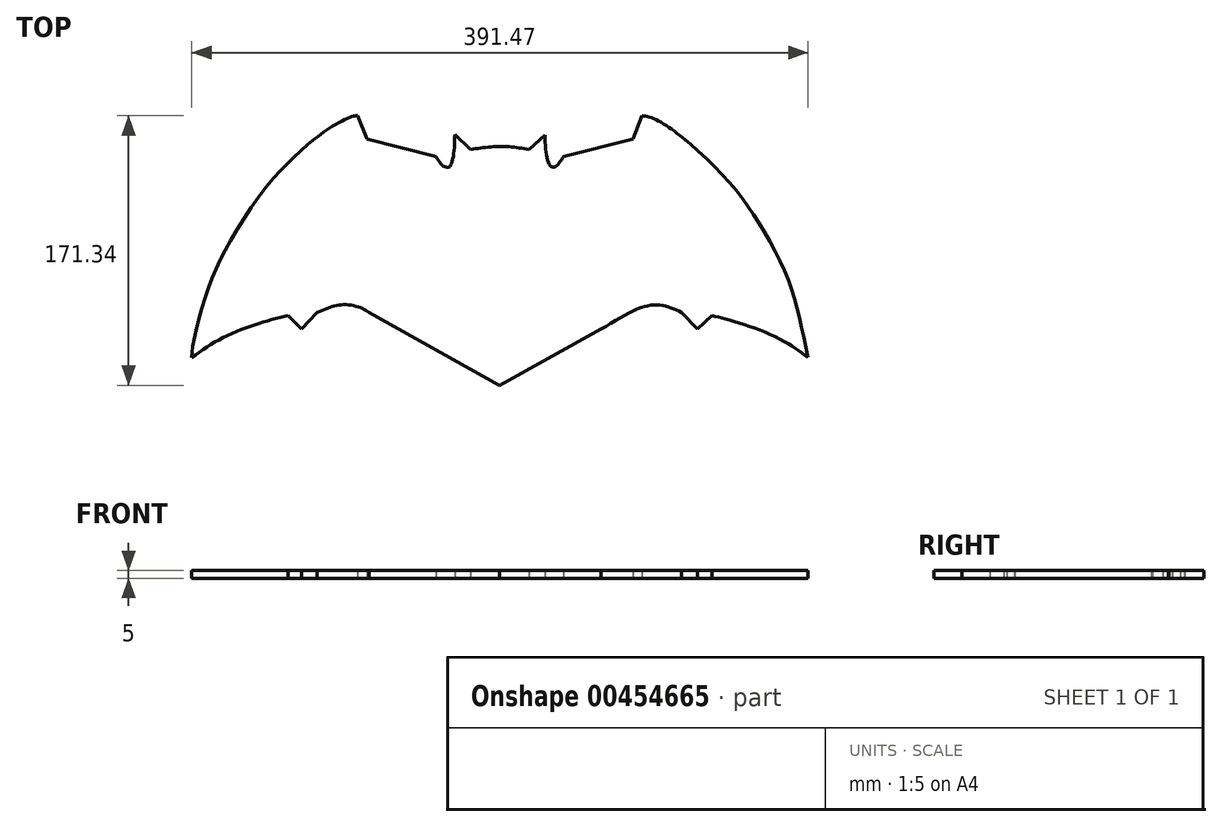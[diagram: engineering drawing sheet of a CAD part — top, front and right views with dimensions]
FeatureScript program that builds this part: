
annotation { "Feature Type Name" : "Feature", "Feature Type Description" : "" }
export const myFeature = defineFeature(function(context is Context, id is Id, definition is map)
    precondition{}
    {
        {
            var Q0;
            Q0=qCreatedBy(makeId("Top.planeOp"),FACE);
            var sketch = newSketch(context, id + "F0", { "sketchPlane" : qUnion([Q0])});
            skLineSegment(sketch, "E0", {"start": v(90.7, 97.95) * mm, "end": v(85.03, 83.2) * mm});
            skLineSegment(sketch, "E1", {"start": v(-84.14, 83.2) * mm, "end": v(-90.13, 97.95) * mm});
            skLineSegment(sketch, "E2", {"start": v(85.03, 83.2) * mm, "end": v(40.87, 72.04) * mm});
            skLineSegment(sketch, "E3", {"start": v(-84.14, 83.2) * mm, "end": v(-40.32, 72.04) * mm});
            skLineSegment(sketch, "E4", {"start": v(-28.3, 85.83) * mm, "end": v(-18.16, 76.47) * mm});
            skLineSegment(sketch, "E5", {"start": v(18.86, 76.47) * mm, "end": v(28.95, 85.66) * mm});
            skLineSegment(sketch, "E6", {"start": v(-125.72, -37.72) * mm, "end": v(-134.3, -29.02) * mm});
            skLineSegment(sketch, "E7", {"start": v(-125.72, -37.72) * mm, "end": v(-115.64, -27.08) * mm});
            skLineSegment(sketch, "E8", {"start": v(-82.75, -27.08) * mm, "end": v(0, -73.39) * mm});
            skLineSegment(sketch, "E9", {"start": v(0, -73.39) * mm, "end": v(0.15, -73.32) * mm});
            skLineSegment(sketch, "E10", {"start": v(0.15, -73.32) * mm, "end": v(64.62, -37.72) * mm});
            skLineSegment(sketch, "E11", {"start": v(115.73, -27.08) * mm, "end": v(125.91, -37.72) * mm});
            skLineSegment(sketch, "E12", {"start": v(135.15, -29.02) * mm, "end": v(125.91, -37.72) * mm});
            skFitSpline(sketch, "E13", {"points": [v(40.87, 72.04) * mm, v(36.7, 66.49) * mm, v(34.09, 65.2) * mm, v(31.14, 68.15) * mm, v(28.95, 85.66) * mm], "startDerivative": vector(-16.96, -25.48) * mm, "endDerivative": vector(-2.16, 52.23) * mm});
            skFitSpline(sketch, "E14", {"points": [v(-18.16, 76.47) * mm, v(-6.02, 78.09) * mm, v(6.53, 78.16) * mm, v(18.86, 76.47) * mm], "startDerivative": vector(36.43, 5.75) * mm, "endDerivative": vector(36.76, -6.17) * mm});
            skFitSpline(sketch, "E15", {"points": [v(-40.32, 72.04) * mm, v(-36.87, 67.11) * mm, v(-34.9, 65.5) * mm, v(-32.23, 65.18) * mm, v(-30.73, 66.87) * mm, v(-28.92, 74) * mm, v(-28.3, 85.83) * mm], "startDerivative": vector(20.16, -30.47) * mm, "endDerivative": vector(0.66, 47.5) * mm});
            skFitSpline(sketch, "E16", {"points": [v(-90.13, 97.95) * mm, v(-94.26, 97.17) * mm, v(-111, 87.88) * mm, v(-126.15, 75.58) * mm], "startDerivative": vector(-18.23, -1.13) * mm, "endDerivative": vector(-34.14, -30.4) * mm});
            skFitSpline(sketch, "E17", {"points": [v(-126.15, 75.58) * mm, v(-146.05, 55.06) * mm, v(-172.4, 15.61) * mm, v(-185.23, -13.1) * mm, v(-194.2, -45.29) * mm, v(-195.41, -55.7) * mm], "startDerivative": vector(-96.65, -89.26) * mm, "endDerivative": vector(-4.24, -72.95) * mm});
            skFitSpline(sketch, "E18", {"points": [v(-195.41, -55.7) * mm, v(-176.06, -43.34) * mm, v(-153.1, -34.14) * mm, v(-134.3, -29.02) * mm], "startDerivative": vector(54.74, 38.6) * mm, "endDerivative": vector(58.58, 14.66) * mm});
            skFitSpline(sketch, "E19", {"points": [v(-115.64, -27.08) * mm, v(-105.81, -23.2) * mm, v(-97.02, -22.13) * mm, v(-87.9, -24.2) * mm, v(-82.75, -27.08) * mm], "startDerivative": vector(35.87, 15.87) * mm, "endDerivative": vector(22.35, -14.72) * mm});
            skFitSpline(sketch, "E20", {"points": [v(64.62, -37.72) * mm, v(88.11, -24.67) * mm, v(99.43, -22.3) * mm, v(108.1, -23.75) * mm, v(115.73, -27.08) * mm], "startDerivative": vector(70.54, 43.38) * mm, "endDerivative": vector(37.26, -18.4) * mm});
            skFitSpline(sketch, "E21", {"points": [v(196.06, -55.7) * mm, v(185.3, -48.1) * mm, v(166.5, -38.7) * mm, v(144.96, -31.52) * mm, v(135.15, -29.02) * mm], "startDerivative": vector(-44.37, 33.65) * mm, "endDerivative": vector(-44.65, 10.71) * mm});
            skFitSpline(sketch, "E22", {"points": [v(90.7, 97.95) * mm, v(96.78, 96.58) * mm, v(110.45, 88.6) * mm, v(126.23, 75.58) * mm], "startDerivative": vector(24.56, -3.16) * mm, "endDerivative": vector(37.58, -33.03) * mm});
            skFitSpline(sketch, "E23", {"points": [v(126.23, 75.58) * mm, v(150.07, 51) * mm, v(165.98, 27.8) * mm, v(181.37, -1) * mm, v(189.84, -27.08) * mm, v(196.06, -55.7) * mm], "startDerivative": vector(120.28, -115.61) * mm, "endDerivative": vector(30.15, -148.28) * mm});
            skSolve(sketch);
        }
        {
            var Q0;
            Q0=makeQuery(id+"F0.imprint","IMPRINT",FACE,{"disambiguationData":[TD([[makeQuery(id+"F0.imprint","IMPRINT",EDGE,{"derivedFrom":sQuery(id+"F0.wireOp",EDGE,"E0")}),1.0]])]});
            extrude(context, id + "F1", {"entities" : qUnion([Q0]), "depth" : 5 * mm});
        }
    });
